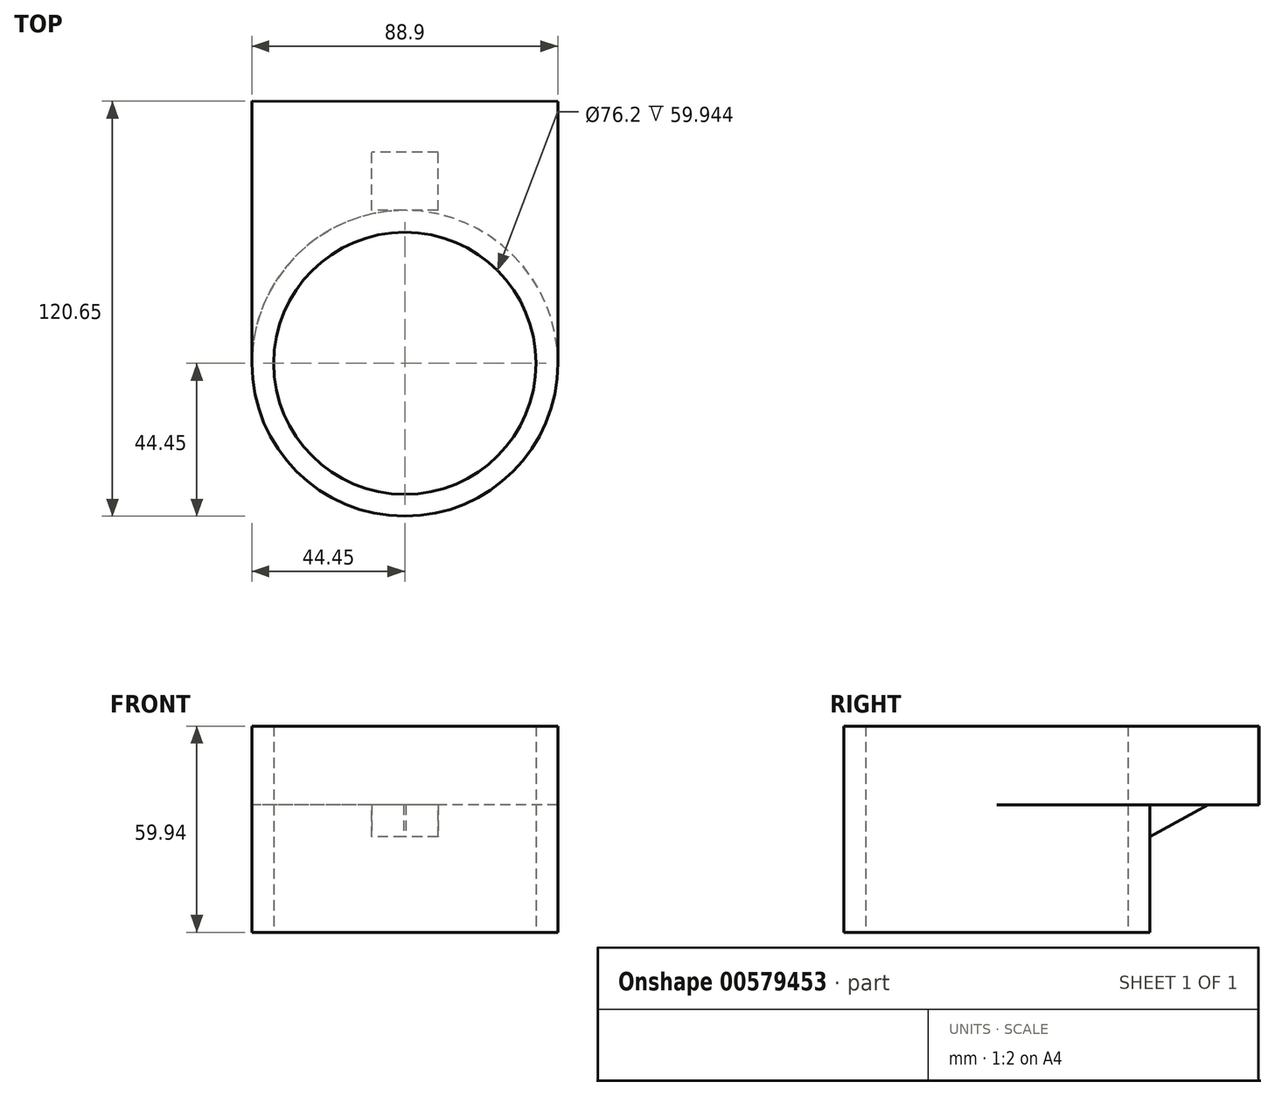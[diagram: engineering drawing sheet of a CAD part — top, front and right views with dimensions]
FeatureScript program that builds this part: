
annotation { "Feature Type Name" : "Feature", "Feature Type Description" : "" }
export const myFeature = defineFeature(function(context is Context, id is Id, definition is map)
    precondition{}
    {
        {
            var Q0;
            Q0=qCreatedBy(makeId("Top.planeOp"),FACE);
            var sketch = newSketch(context, id + "F0", { "sketchPlane" : qUnion([Q0])});
            skCircle(sketch, "E0", {"center": v(0, 0) * mm, "radius": 44.45 * mm});
            skCircle(sketch, "E1", {"center": v(0, 0) * mm, "radius": 38.1 * mm});
            skSolve(sketch);
        }
        {
            var Q0;
            Q0=makeQuery(id+"F0.imprint","IMPRINT",FACE,{"disambiguationData":[TD([[makeQuery(id+"F0.imprint","IMPRINT",EDGE,{"derivedFrom":sQuery(id+"F0.wireOp",EDGE,"E0")}),1.0]])]});
            extrude(context, id + "F1", {"entities" : qUnion([Q0]), "depth" : 59.94 * mm, "offsetDistance" : 25.4 * mm});
        }
        {
            var Q0;
            Q0=makeQuery(id+"F1.opExtrude","CAP_FACE",FACE,{"disambiguationData":[OSD([sQuery(id+"F0.wireOp",EDGE,"E0"),sQuery(id+"F0.wireOp",EDGE,"E1")])],"isStart":false});
            var sketch = newSketch(context, id + "F2", { "sketchPlane" : qUnion([Q0])});
            skLineSegment(sketch, "E2", {"start": v(-44.45, 0) * mm, "end": v(-44.45, 76.2) * mm});
            skLineSegment(sketch, "E3", {"start": v(44.45, 0) * mm, "end": v(44.45, 76.15) * mm});
            skLineSegment(sketch, "E4", {"start": v(44.45, 76.15) * mm, "end": v(-44.45, 76.2) * mm});
            skSolve(sketch);
        }
        {
            var Q0;
            {var subQ0=sQuery(id+"F2.wireOp",EDGE,"E2");Q0=makeQuery(id+"F2.imprint","IMPRINT",FACE,{"disambiguationData":[TD([[makeQuery(id+"F2.imprint","IMPRINT",EDGE,{"derivedFrom":subQ0}),-1.0]])]});}
            extrude(context, id + "F3", {"entities" : qUnion([Q0]), "operationType" : NewBodyOperationType.ADD, "oppositeDirection" : true, "depth" : 22.86 * mm, "offsetDistance" : 25.4 * mm});
        }
        {
            var Q0;
            Q0=qCreatedBy(makeId("Right.planeOp"),FACE);
            var sketch = newSketch(context, id + "F4", { "sketchPlane" : qUnion([Q0])});
            skLineSegment(sketch, "E5", {"start": v(44.45, 37.08) * mm, "end": v(61.35, 37.08) * mm});
            skLineSegment(sketch, "E6", {"start": v(44.45, 37.08) * mm, "end": v(44.45, 27.73) * mm});
            skLineSegment(sketch, "E7", {"start": v(44.45, 27.73) * mm, "end": v(61.35, 37.08) * mm});
            skSolve(sketch);
        }
        {
            var Q0;
            Q0=makeQuery(id+"F4.imprint","IMPRINT",FACE,{"disambiguationData":[TD([[makeQuery(id+"F4.imprint","IMPRINT",EDGE,{"derivedFrom":sQuery(id+"F4.wireOp",EDGE,"E5")}),-1.0]])]});
            extrude(context, id + "F5", {"entities" : qUnion([Q0]), "operationType" : NewBodyOperationType.ADD, "endBound" : BoundingType.SYMMETRIC, "depth" : 19.3 * mm, "offsetDistance" : 25.4 * mm});
        }
    });
